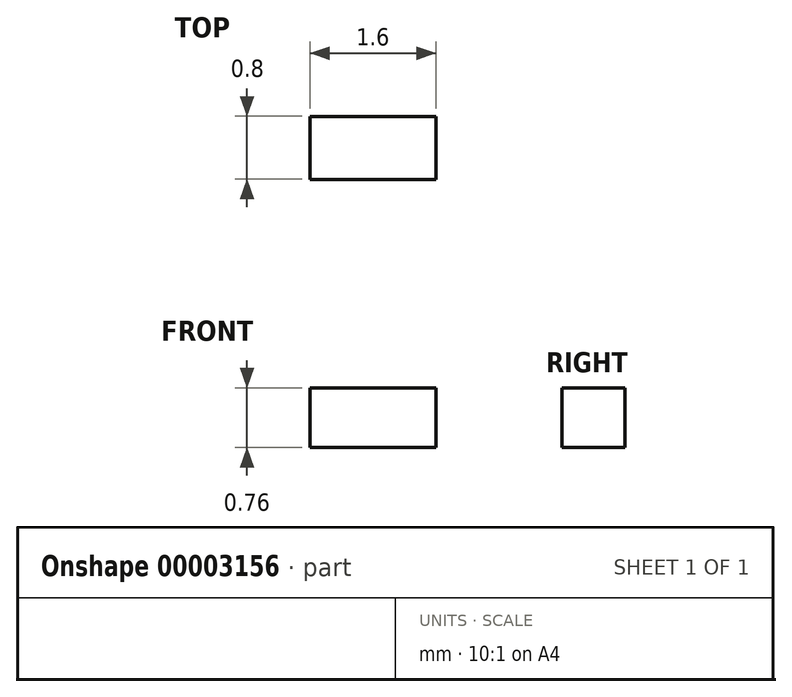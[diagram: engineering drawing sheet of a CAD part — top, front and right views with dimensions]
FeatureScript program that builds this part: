
annotation { "Feature Type Name" : "Feature", "Feature Type Description" : "" }
export const myFeature = defineFeature(function(context is Context, id is Id, definition is map)
    precondition{}
    {
        {
            var Q0;
            Q0=qCreatedBy(makeId("Top.planeOp"),FACE);
            var sketch = newSketch(context, id + "F0", { "sketchPlane" : qUnion([Q0])});
            skLineSegment(sketch, "E0.bottom", {"start": v(0.24, -1.23) * mm, "end": v(1.84, -1.23) * mm});
            skLineSegment(sketch, "E0.top", {"start": v(0.24, -2.03) * mm, "end": v(1.84, -2.03) * mm});
            skLineSegment(sketch, "E0.left", {"start": v(0.24, -1.23) * mm, "end": v(0.24, -2.03) * mm});
            skLineSegment(sketch, "E0.right", {"start": v(1.84, -1.23) * mm, "end": v(1.84, -2.03) * mm});
            skSolve(sketch);
        }
        {
            var Q0;
            Q0=makeQuery(id+"F0.imprint","IMPRINT",FACE,{"disambiguationData":[TD([[makeQuery(id+"F0.imprint","IMPRINT",EDGE,{"derivedFrom":sQuery(id+"F0.wireOp",EDGE,"E0.bottom")}),-1.0]])]});
            extrude(context, id + "F1", {"entities" : qUnion([Q0]), "depth" : .76 * mm});
        }
    });
